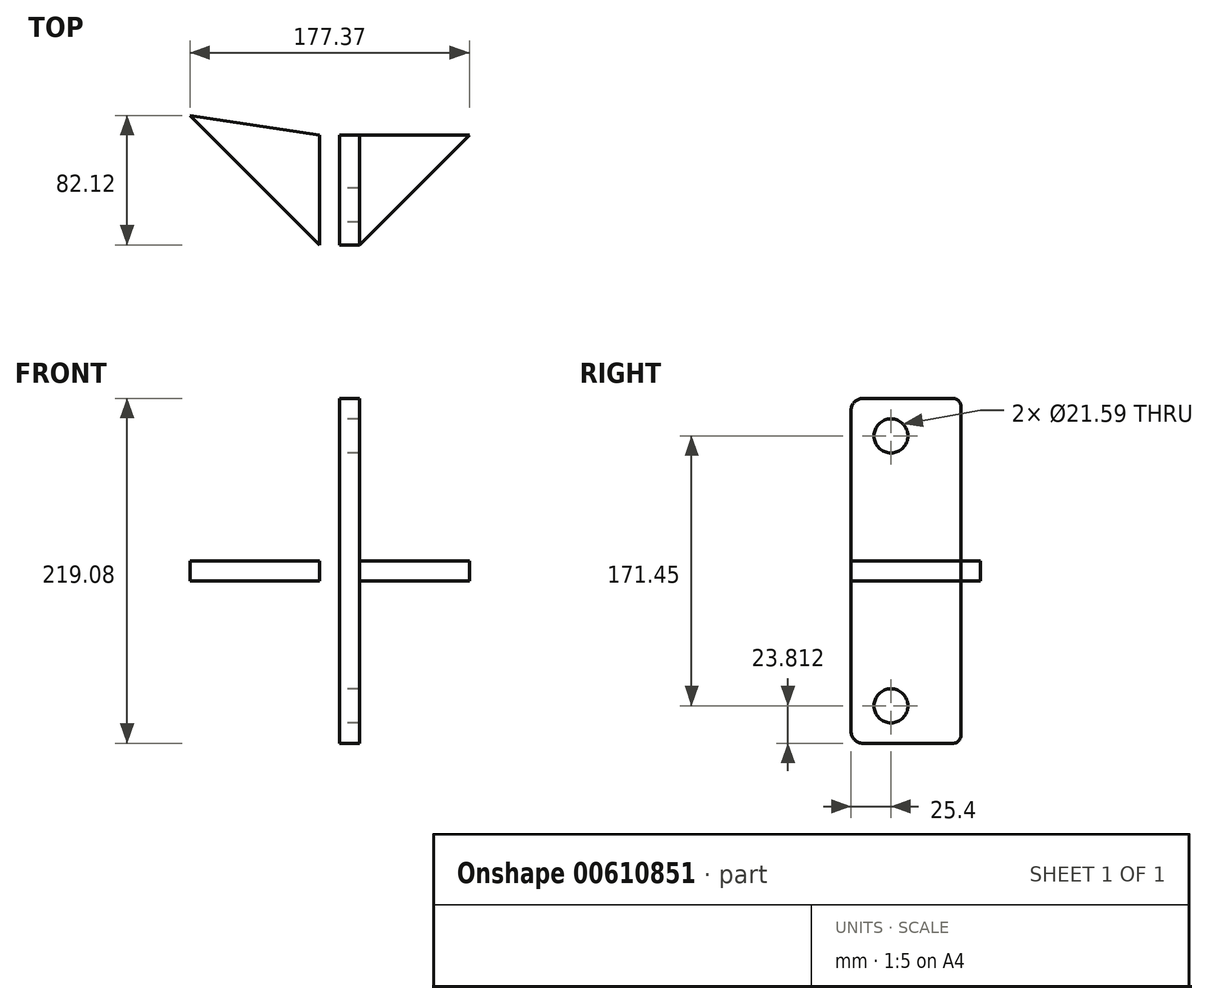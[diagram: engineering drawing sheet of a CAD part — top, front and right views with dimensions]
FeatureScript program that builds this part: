
annotation { "Feature Type Name" : "Feature", "Feature Type Description" : "" }
export const myFeature = defineFeature(function(context is Context, id is Id, definition is map)
    precondition{}
    {
        {
            var Q0;
            Q0=qCreatedBy(makeId("Right.planeOp"),FACE);
            var sketch = newSketch(context, id + "F0", { "sketchPlane" : qUnion([Q0])});
            skLineSegment(sketch, "E0.bottom", {"start": v(0, 0) * mm, "end": v(69.85, 0) * mm});
            skLineSegment(sketch, "E0.top", {"start": v(0, 219.08) * mm, "end": v(69.85, 219.08) * mm});
            skLineSegment(sketch, "E0.left", {"start": v(0, 0) * mm, "end": v(0, 219.08) * mm});
            skLineSegment(sketch, "E0.right", {"start": v(69.85, 0) * mm, "end": v(69.85, 219.08) * mm});
            skCircle(sketch, "E1", {"center": v(25.4, 195.26) * mm, "radius": 10.8 * mm});
            skCircle(sketch, "E2", {"center": v(25.4, 23.81) * mm, "radius": 10.8 * mm});
            skLineSegment(sketch, "E3", {"start": v(25.4, 195.26) * mm, "end": v(25.4, 23.81) * mm, "construction": true});
            skPoint(sketch, "E4", {"position": v(0, 109.54) * mm});
            skPoint(sketch, "E5", {"position": v(25.4, 109.54) * mm});
            skSolve(sketch);
        }
        {
            var Q0;
            Q0 = qSketchRegion(id + "F0", true);
            extrude(context, id + "F1", {"entities" : qUnion([Q0]), "depth" : 12.7 * mm, "offsetDistance" : 25.4 * mm});
        }
        {
            var Q0;
            Q0=makeQuery(id+"F1.opExtrude","SWEPT_EDGE",EDGE,{"disambiguationData":[OSD([sQuery(id+"F0.wireOp",EDGE,"E0.top"),sQuery(id+"F0.wireOp",EDGE,"E0.right")])]});
            var Q1;
            Q1=makeQuery(id+"F1.opExtrude","SWEPT_EDGE",EDGE,{"disambiguationData":[OSD([sQuery(id+"F0.wireOp",EDGE,"E0.bottom"),sQuery(id+"F0.wireOp",EDGE,"E0.right")])]});
            fillet(context, id + "F2", {"entities" : qUnion([Q0, Q1]), "tangentPropagation" : true, "radius" : 5.08 * mm, "defaultsChanged" : false, "vertexSettings" : [], "allowEdgeOverflow" : false});
        }
        {
            var Q0;
            Q0=makeQuery(id+"F1.opExtrude","SWEPT_EDGE",EDGE,{"disambiguationData":[OSD([sQuery(id+"F0.wireOp",EDGE,"E0.top"),sQuery(id+"F0.wireOp",EDGE,"E0.left")])]});
            var Q1;
            Q1=makeQuery(id+"F1.opExtrude","SWEPT_EDGE",EDGE,{"disambiguationData":[OSD([sQuery(id+"F0.wireOp",EDGE,"E0.bottom"),sQuery(id+"F0.wireOp",EDGE,"E0.left")])]});
            fillet(context, id + "F3", {"entities" : qUnion([Q0, Q1]), "tangentPropagation" : true, "radius" : 7.62 * mm, "defaultsChanged" : true, "vertexSettings" : [], "allowEdgeOverflow" : false});
        }
        {
            var Q0;
            Q0=makeQuery(id+"F1.opExtrude","CAP_FACE",FACE,{"disambiguationData":[OSD([sQuery(id+"F0.wireOp",EDGE,"E0.bottom"),sQuery(id+"F0.wireOp",EDGE,"E0.top"),sQuery(id+"F0.wireOp",EDGE,"E0.left"),sQuery(id+"F0.wireOp",EDGE,"E0.right"),sQuery(id+"F0.wireOp",EDGE,"E1"),sQuery(id+"F0.wireOp",EDGE,"E2")])],"isStart":false});
            var sketch = newSketch(context, id + "F4", { "sketchPlane" : qUnion([Q0])});
            skLineSegment(sketch, "E6.bottom", {"start": v(0, 115.89) * mm, "end": v(69.85, 115.89) * mm});
            skLineSegment(sketch, "E6.top", {"start": v(0, 103.19) * mm, "end": v(69.85, 103.19) * mm});
            skLineSegment(sketch, "E6.left", {"start": v(0, 115.89) * mm, "end": v(0, 103.19) * mm});
            skLineSegment(sketch, "E6.right", {"start": v(69.85, 115.89) * mm, "end": v(69.85, 103.19) * mm});
            skLineSegment(sketch, "E7", {"start": v(0, 109.54) * mm, "end": v(69.85, 109.54) * mm, "construction": true});
            skSolve(sketch);
        }
        {
            var Q0;
            Q0 = qSketchRegion(id + "F4", true);
            extrude(context, id + "F5", {"entities" : qUnion([Q0]), "depth" : 69.85 * mm, "offsetDistance" : 25.4 * mm});
        }
        {
            var Q0;
            Q0=makeQuery(id+"F5.opExtrude","SWEPT_FACE",FACE,{"disambiguationData":[OSD([sQuery(id+"F4.wireOp",EDGE,"E6.bottom")])]});
            var sketch = newSketch(context, id + "F6", { "sketchPlane" : qUnion([Q0])});
            skLineSegment(sketch, "E8", {"start": v(82.55, 69.85) * mm, "end": v(12.7, 0) * mm});
            skLineSegment(sketch, "E9", {"start": v(12.7, 0) * mm, "end": v(82.55, 0) * mm});
            skLineSegment(sketch, "E10", {"start": v(82.55, 0) * mm, "end": v(82.55, 69.85) * mm});
            skSolve(sketch);
        }
        {
            var Q0;
            Q0 = qSketchRegion(id + "F6", true);
            extrude(context, id + "F7", {"entities" : qUnion([Q0]), "operationType" : NewBodyOperationType.REMOVE, "endBound" : BoundingType.THROUGH_ALL, "oppositeDirection" : true, "depth" : 25.4 * mm, "offsetDistance" : 25.4 * mm});
        }
        {
            var Q0;
            Q0=makeQuery(id+"F5.opExtrude","SWEPT_BODY",BODY,{"disambiguationData":[OSD([sQuery(id+"F4.wireOp",EDGE,"E6.bottom"),sQuery(id+"F4.wireOp",EDGE,"E6.top"),sQuery(id+"F4.wireOp",EDGE,"E6.left"),sQuery(id+"F4.wireOp",EDGE,"E6.right")])]});
            var Q1;
            Q1=makeQuery(id+"F1.opExtrude","CAP_FACE",FACE,{"disambiguationData":[OSD([sQuery(id+"F0.wireOp",EDGE,"E0.bottom"),sQuery(id+"F0.wireOp",EDGE,"E0.top"),sQuery(id+"F0.wireOp",EDGE,"E0.left"),sQuery(id+"F0.wireOp",EDGE,"E0.right"),sQuery(id+"F0.wireOp",EDGE,"E1"),sQuery(id+"F0.wireOp",EDGE,"E2")])],"isStart":true});
            mirror(context, id + "F8", {"entities" : qUnion([Q0]), "mirrorPlane" : qUnion([Q1])});
        }
        {
            var Q0;
            Q0=makeQuery(id+"F8.opPattern","COPY",FACE,{"derivedFrom":makeQuery(id+"F5.opExtrude","SWEPT_FACE",FACE,{"disambiguationData":[OSD([sQuery(id+"F4.wireOp",EDGE,"E6.bottom")])]}),"instanceName":"1"});
            var sketch = newSketch(context, id + "F9", { "sketchPlane" : qUnion([Q0])});
            skLineSegment(sketch, "E11", {"start": v(-12.7, 69.85) * mm, "end": v(-94.82, 82.12) * mm});
            skLineSegment(sketch, "E12", {"start": v(-94.82, 82.12) * mm, "end": v(-82.55, 69.85) * mm});
            skLineSegment(sketch, "E13", {"start": v(-82.55, 69.85) * mm, "end": v(-12.7, 69.85) * mm});
            skSolve(sketch);
        }
        {
            var Q0;
            Q0 = qSketchRegion(id + "F9", true);
            var Q1;
            Q1=makeQuery(id+"F8.opPattern","COPY",FACE,{"derivedFrom":makeQuery(id+"F5.opExtrude","SWEPT_FACE",FACE,{"disambiguationData":[OSD([sQuery(id+"F4.wireOp",EDGE,"E6.top")])]}),"instanceName":"1"});
            extrude(context, id + "F10", {"entities" : qUnion([Q0]), "operationType" : NewBodyOperationType.ADD, "endBound" : BoundingType.UP_TO_SURFACE, "oppositeDirection" : true, "depth" : 25.4 * mm, "endBoundEntityFace" : qUnion([Q1]), "offsetDistance" : 25.4 * mm});
        }
    });
